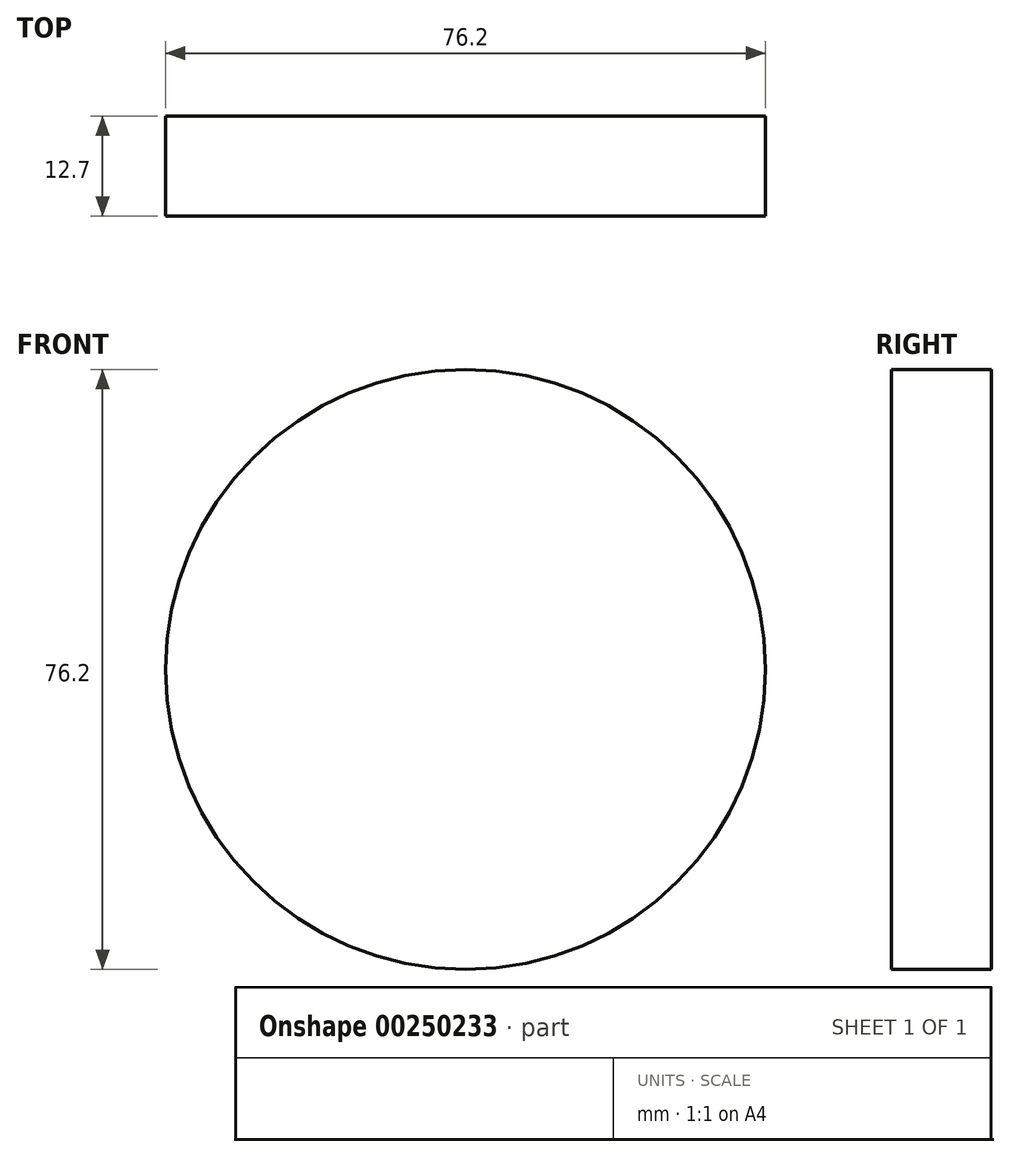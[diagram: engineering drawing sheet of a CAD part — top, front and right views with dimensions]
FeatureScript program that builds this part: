
annotation { "Feature Type Name" : "Feature", "Feature Type Description" : "" }
export const myFeature = defineFeature(function(context is Context, id is Id, definition is map)
    precondition{}
    {
        {
            var Q0;
            Q0=qCreatedBy(makeId("Front.planeOp"),FACE);
            var sketch = newSketch(context, id + "F0", { "sketchPlane" : qUnion([Q0])});
            skCircle(sketch, "E0", {"center": v(0, 0) * mm, "radius": 38.1 * mm});
            skCircle(sketch, "E1", {"center": v(-61.02, 0) * mm, "radius": 44.45 * mm});
            skSolve(sketch);
        }
        {
            var Q0;
            {var subQ0=sQuery(id+"F0.wireOp",EDGE,"E1");var subQ1=sQuery(id+"F0.wireOp",EDGE,"E0");var subQ2=makeQuery(id+"F0.imprint","INTERSECT",VERTEX,{"disambiguationData":[OD(0.0)],"derivedFrom":[subQ1,subQ0]});Q0=makeQuery(id+"F0.imprint","IMPRINT",FACE,{"disambiguationData":[TD([[makeQuery(id+"F0.imprint","IMPRINT",EDGE,{"disambiguationData":[TD([[subQ2,-1.0]])],"derivedFrom":subQ1}),1.0]])]});}
            var Q1;
            {var subQ0=sQuery(id+"F0.wireOp",EDGE,"E1");var subQ1=sQuery(id+"F0.wireOp",EDGE,"E0");var subQ2=makeQuery(id+"F0.imprint","INTERSECT",VERTEX,{"disambiguationData":[OD(0.0)],"derivedFrom":[subQ1,subQ0]});Q1=makeQuery(id+"F0.imprint","IMPRINT",FACE,{"disambiguationData":[TD([[makeQuery(id+"F0.imprint","IMPRINT",EDGE,{"disambiguationData":[TD([[subQ2,1.0]])],"derivedFrom":subQ1}),1.0]])]});}
            extrude(context, id + "F1", {"entities" : qUnion([Q0, Q1]), "depth" : 12.7 * mm});
        }
    });
